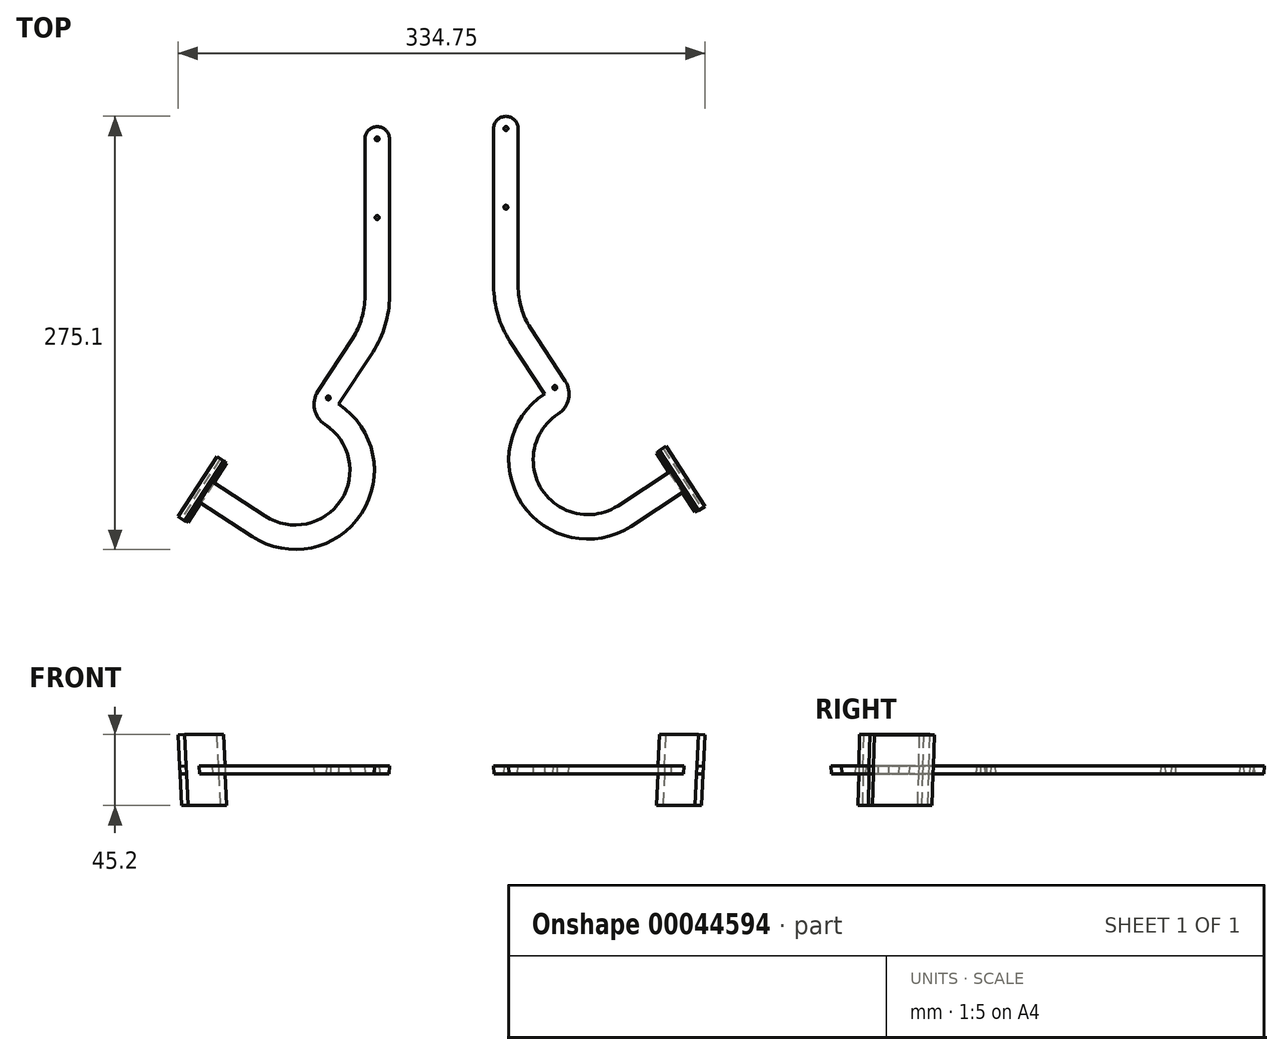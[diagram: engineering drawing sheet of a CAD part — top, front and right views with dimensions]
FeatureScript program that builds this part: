
annotation { "Feature Type Name" : "Feature", "Feature Type Description" : "" }
export const myFeature = defineFeature(function(context is Context, id is Id, definition is map)
    precondition{}
    {
        {
            var Q0;
            Q0=qCreatedBy(makeId("Top.planeOp"),FACE);
            var sketch = newSketch(context, id + "F0", { "sketchPlane" : qUnion([Q0])});
            skLineSegment(sketch, "E0", {"start": v(34.03, 89.45) * mm, "end": v(34.03, -10.55) * mm});
            skArc(sketch, "E1", {"start": v(34.03, -10.55) * mm, "mid": v(36.7, -28.86) * mm, "end": v(44.46, -45.66) * mm});
            skLineSegment(sketch, "E2", {"start": v(44.46, -45.66) * mm, "end": v(66.3, -79.17) * mm});
            skLineSegment(sketch, "E3", {"start": v(66.3, -79.17) * mm, "end": v(78.87, -70.98) * mm});
            skLineSegment(sketch, "E4", {"start": v(44.46, -45.66) * mm, "end": v(57.03, -37.47) * mm});
            skLineSegment(sketch, "E5", {"start": v(57.03, -37.47) * mm, "end": v(78.87, -70.98) * mm});
            skLineSegment(sketch, "E6", {"start": v(34.03, 89.45) * mm, "end": v(49.03, 89.45) * mm});
            skLineSegment(sketch, "E7", {"start": v(34.03, -10.55) * mm, "end": v(49.03, -10.55) * mm});
            skLineSegment(sketch, "E8", {"start": v(49.03, 89.45) * mm, "end": v(49.03, -10.55) * mm});
            skArc(sketch, "E9", {"start": v(49.03, -10.55) * mm, "mid": v(51.07, -24.6) * mm, "end": v(57.03, -37.47) * mm});
            skArc(sketch, "E10", {"start": v(49.03, 89.45) * mm, "mid": v(41.53, 96.95) * mm, "end": v(34.03, 89.45) * mm});
            skLineSegment(sketch, "E11", {"start": v(-32.73, 82.88) * mm, "end": v(-32.73, -17.12) * mm});
            skLineSegment(sketch, "E12", {"start": v(-32.73, 82.88) * mm, "end": v(-47.73, 82.88) * mm});
            skArc(sketch, "E13", {"start": v(-32.73, 82.88) * mm, "mid": v(-40.23, 90.38) * mm, "end": v(-47.73, 82.88) * mm});
            skLineSegment(sketch, "E14", {"start": v(-47.73, 82.88) * mm, "end": v(-47.73, -17.12) * mm});
            skLineSegment(sketch, "E15", {"start": v(-47.73, -17.12) * mm, "end": v(-32.73, -17.12) * mm});
            skArc(sketch, "E16", {"start": v(-32.73, -17.12) * mm, "mid": v(-35.39, -35.43) * mm, "end": v(-43.16, -52.23) * mm});
            skLineSegment(sketch, "E17", {"start": v(-43.16, -52.23) * mm, "end": v(-65, -85.74) * mm});
            skLineSegment(sketch, "E18", {"start": v(-65, -85.74) * mm, "end": v(-77.57, -77.55) * mm});
            skLineSegment(sketch, "E19", {"start": v(-43.16, -52.23) * mm, "end": v(-55.72, -44.04) * mm});
            skLineSegment(sketch, "E20", {"start": v(-55.72, -44.04) * mm, "end": v(-77.57, -77.55) * mm});
            skArc(sketch, "E21", {"start": v(-55.72, -44.04) * mm, "mid": v(-49.77, -31.16) * mm, "end": v(-47.73, -17.12) * mm});
            skPoint(sketch, "E22", {"position": v(-20.89, 95.2) * mm});
            skCircle(sketch, "E23", {"center": v(-40.23, 82.88) * mm, "radius": 1.5 * mm});
            skCircle(sketch, "E24", {"center": v(-71.28, -81.64) * mm, "radius": 1.5 * mm});
            skLineSegment(sketch, "E25", {"start": v(-40.23, 82.88) * mm, "end": v(-40.23, 32.88) * mm});
            skCircle(sketch, "E26", {"center": v(-40.23, 32.88) * mm, "radius": 1.5 * mm});
            skCircle(sketch, "E27", {"center": v(41.53, 89.45) * mm, "radius": 1.5 * mm});
            skLineSegment(sketch, "E28", {"start": v(41.53, 89.45) * mm, "end": v(41.53, 39.45) * mm});
            skCircle(sketch, "E29", {"center": v(41.53, 39.45) * mm, "radius": 1.5 * mm});
            skCircle(sketch, "E30", {"center": v(72.59, -75.08) * mm, "radius": 1.5 * mm});
            skLineSegment(sketch, "E31", {"start": v(-65, -85.74) * mm, "end": v(-73.19, -98.3) * mm});
            skArc(sketch, "E32", {"start": v(-77.57, -77.55) * mm, "mid": v(-79.68, -88.83) * mm, "end": v(-73.19, -98.3) * mm});
            skLineSegment(sketch, "E33", {"start": v(-73.19, -98.3) * mm, "end": v(-111.41, -156.95) * mm});
            skLineSegment(sketch, "E34", {"start": v(-111.41, -156.95) * mm, "end": v(-119.6, -169.51) * mm});
            skLineSegment(sketch, "E35", {"start": v(-111.41, -156.95) * mm, "end": v(-144.92, -135.1) * mm});
            skLineSegment(sketch, "E36", {"start": v(-144.92, -135.1) * mm, "end": v(-153.11, -147.67) * mm});
            skLineSegment(sketch, "E37", {"start": v(-119.6, -169.51) * mm, "end": v(-153.11, -147.67) * mm});
            skArc(sketch, "E38", {"start": v(-119.6, -169.51) * mm, "mid": v(-50.41, -154.93) * mm, "end": v(-65, -85.74) * mm});
            skArc(sketch, "E39", {"start": v(-111.41, -156.95) * mm, "mid": v(-62.98, -146.74) * mm, "end": v(-73.19, -98.3) * mm});
            skLineSegment(sketch, "E40", {"start": v(66.3, -79.17) * mm, "end": v(74.5, -91.74) * mm});
            skArc(sketch, "E41", {"start": v(74.5, -91.74) * mm, "mid": v(80.98, -82.27) * mm, "end": v(78.87, -70.98) * mm});
            skLineSegment(sketch, "E42", {"start": v(74.5, -91.74) * mm, "end": v(112.72, -150.38) * mm});
            skLineSegment(sketch, "E43", {"start": v(112.72, -150.38) * mm, "end": v(146.23, -128.54) * mm});
            skLineSegment(sketch, "E44", {"start": v(112.72, -150.38) * mm, "end": v(120.9, -162.95) * mm});
            skLineSegment(sketch, "E45", {"start": v(120.9, -162.95) * mm, "end": v(154.42, -141.1) * mm});
            skLineSegment(sketch, "E46", {"start": v(146.23, -128.54) * mm, "end": v(154.42, -141.1) * mm});
            skArc(sketch, "E47", {"start": v(66.3, -79.17) * mm, "mid": v(51.72, -148.36) * mm, "end": v(120.9, -162.95) * mm});
            skArc(sketch, "E48", {"start": v(74.5, -91.74) * mm, "mid": v(64.28, -140.17) * mm, "end": v(112.72, -150.38) * mm});
            skSolve(sketch);
        }
        {
            var Q0;
            {var subQ0=sQuery(id+"F0.wireOp",EDGE,"E13");Q0=makeQuery(id+"F0.imprint","IMPRINT",FACE,{"disambiguationData":[TD([[makeQuery(id+"F0.imprint","IMPRINT",EDGE,{"derivedFrom":subQ0}),1.0]])]});}
            var Q1;
            {var subQ4=sQuery(id+"F0.wireOp",EDGE,"E11");Q1=makeQuery(id+"F0.imprint","IMPRINT",FACE,{"disambiguationData":[TD([[makeQuery(id+"F0.imprint","IMPRINT",EDGE,{"derivedFrom":subQ4}),-1.0]])]});}
            var Q2;
            Q2=makeQuery(id+"F0.imprint","IMPRINT",FACE,{"disambiguationData":[TD([[makeQuery(id+"F0.imprint","IMPRINT",EDGE,{"derivedFrom":sQuery(id+"F0.wireOp",EDGE,"E15")}),-1.0]])]});
            var Q3;
            {var subQ5=sQuery(id+"F0.wireOp",EDGE,"E17");Q3=makeQuery(id+"F0.imprint","IMPRINT",FACE,{"disambiguationData":[TD([[makeQuery(id+"F0.imprint","IMPRINT",EDGE,{"derivedFrom":subQ5}),-1.0]])]});}
            var Q4;
            {var subQ4=sQuery(id+"F0.wireOp",EDGE,"E31");Q4=makeQuery(id+"F0.imprint","IMPRINT",FACE,{"disambiguationData":[TD([[makeQuery(id+"F0.imprint","IMPRINT",EDGE,{"derivedFrom":subQ4}),-1.0]])]});}
            var Q5;
            Q5=makeQuery(id+"F0.imprint","IMPRINT",FACE,{"disambiguationData":[TD([[makeQuery(id+"F0.imprint","IMPRINT",EDGE,{"derivedFrom":sQuery(id+"F0.wireOp",EDGE,"E31")}),1.0]])]});
            var Q6;
            Q6=makeQuery(id+"F0.imprint","IMPRINT",FACE,{"disambiguationData":[TD([[makeQuery(id+"F0.imprint","IMPRINT",EDGE,{"derivedFrom":sQuery(id+"F0.wireOp",EDGE,"E34")}),-1.0]])]});
            var Q7;
            {var subQ4=sQuery(id+"F0.wireOp",EDGE,"E10");Q7=makeQuery(id+"F0.imprint","IMPRINT",FACE,{"disambiguationData":[TD([[makeQuery(id+"F0.imprint","IMPRINT",EDGE,{"derivedFrom":subQ4}),1.0]])]});}
            var Q8;
            {var subQ6=sQuery(id+"F0.wireOp",EDGE,"E0");Q8=makeQuery(id+"F0.imprint","IMPRINT",FACE,{"disambiguationData":[TD([[makeQuery(id+"F0.imprint","IMPRINT",EDGE,{"derivedFrom":subQ6}),1.0]])]});}
            var Q9;
            Q9=makeQuery(id+"F0.imprint","IMPRINT",FACE,{"disambiguationData":[TD([[makeQuery(id+"F0.imprint","IMPRINT",EDGE,{"derivedFrom":sQuery(id+"F0.wireOp",EDGE,"E1")}),1.0]])]});
            var Q10;
            {var subQ1=sQuery(id+"F0.wireOp",EDGE,"E2");Q10=makeQuery(id+"F0.imprint","IMPRINT",FACE,{"disambiguationData":[TD([[makeQuery(id+"F0.imprint","IMPRINT",EDGE,{"derivedFrom":subQ1}),1.0]])]});}
            var Q11;
            {var subQ3=sQuery(id+"F0.wireOp",EDGE,"E40");Q11=makeQuery(id+"F0.imprint","IMPRINT",FACE,{"disambiguationData":[TD([[makeQuery(id+"F0.imprint","IMPRINT",EDGE,{"derivedFrom":subQ3}),1.0]])]});}
            var Q12;
            Q12=makeQuery(id+"F0.imprint","IMPRINT",FACE,{"disambiguationData":[TD([[makeQuery(id+"F0.imprint","IMPRINT",EDGE,{"derivedFrom":sQuery(id+"F0.wireOp",EDGE,"E40")}),-1.0]])]});
            var Q13;
            Q13=makeQuery(id+"F0.imprint","IMPRINT",FACE,{"disambiguationData":[TD([[makeQuery(id+"F0.imprint","IMPRINT",EDGE,{"derivedFrom":sQuery(id+"F0.wireOp",EDGE,"E43")}),-1.0]])]});
            extrude(context, id + "F1", {"entities" : qUnion([Q0, Q1, Q2, Q3, Q4, Q5, Q6, Q7, Q8, Q9, Q10, Q11, Q12, Q13]), "depth" : 5 * mm, "hasDraft" : true, "draftAngle" : 3 * degree});
        }
        {
            var Q0;
            Q0=makeQuery(id+"F1.opExtrude","SWEPT_FACE",FACE,{"disambiguationData":[OSD([sQuery(id+"F0.wireOp",EDGE,"E46")])]});
            var sketch = newSketch(context, id + "F2", { "sketchPlane" : qUnion([Q0])});
            skLineSegment(sketch, "E49", {"start": v(-186.9, 14.12) * mm, "end": v(-171.9, 13.61) * mm});
            skLineSegment(sketch, "E50", {"start": v(-202.41, 14.65) * mm, "end": v(-217.4, 15.17) * mm});
            skLineSegment(sketch, "E51", {"start": v(-187.33, 9.13) * mm, "end": v(-172.34, 8.62) * mm});
            skLineSegment(sketch, "E52", {"start": v(-202.32, 9.64) * mm, "end": v(-217.31, 10.15) * mm});
            skLineSegment(sketch, "E53", {"start": v(-171.9, 13.61) * mm, "end": v(-171.22, 33.6) * mm});
            skLineSegment(sketch, "E54", {"start": v(-171.22, 33.6) * mm, "end": v(-216.72, 35.15) * mm});
            skLineSegment(sketch, "E55", {"start": v(-217.4, 15.17) * mm, "end": v(-216.72, 35.15) * mm});
            skLineSegment(sketch, "E56", {"start": v(-172.34, 8.62) * mm, "end": v(-173.02, -11.37) * mm});
            skLineSegment(sketch, "E57", {"start": v(-173.02, -11.37) * mm, "end": v(-218, -9.84) * mm});
            skLineSegment(sketch, "E58", {"start": v(-217.31, 10.15) * mm, "end": v(-218, -9.84) * mm});
            skLineSegment(sketch, "E59", {"start": v(-217.4, 15.17) * mm, "end": v(-217.31, 10.15) * mm});
            skLineSegment(sketch, "E60", {"start": v(-171.9, 13.61) * mm, "end": v(-172.34, 8.62) * mm});
            skSolve(sketch);
        }
        {
            var Q0;
            Q0=makeQuery(id+"F2.imprint","IMPRINT",FACE,{"disambiguationData":[TD([[makeQuery(id+"F2.imprint","IMPRINT",EDGE,{"derivedFrom":sQuery(id+"F2.wireOp",EDGE,"E49")}),1.0]])]});
            var Q1;
            Q1=makeQuery(id+"F2.imprint","IMPRINT",FACE,{"disambiguationData":[TD([[makeQuery(id+"F2.imprint","IMPRINT",EDGE,{"derivedFrom":sQuery(id+"F2.wireOp",EDGE,"E50")}),1.0]])]});
            var Q2;
            Q2=makeQuery(id+"F2.imprint","IMPRINT",FACE,{"disambiguationData":[TD([[makeQuery(id+"F2.imprint","IMPRINT",EDGE,{"derivedFrom":sQuery(id+"F2.wireOp",EDGE,"E49")}),-1.0]])]});
            var Q3;
            {var subQ0=sQuery(id+"F0.wireOp",EDGE,"E46");Q3=makeQuery(id+"F2.imprint","IMPRINT",FACE,{"disambiguationData":[TD([[makeQuery(id+"F2.imprint","IMPRINT",EDGE,{"derivedFrom":makeQuery(id+"F1.opExtrude","CAP_EDGE",EDGE,{"disambiguationData":[OSD([subQ0])],"isStart":true})}),-1.0]])]});}
            var Q4;
            Q4=makeQuery(id+"F2.imprint","IMPRINT",FACE,{"disambiguationData":[TD([[makeQuery(id+"F2.imprint","IMPRINT",EDGE,{"derivedFrom":sQuery(id+"F2.wireOp",EDGE,"E51")}),-1.0]])]});
            extrude(context, id + "F3", {"entities" : qUnion([Q0, Q1, Q2, Q3, Q4]), "operationType" : NewBodyOperationType.ADD, "depth" : 5 * mm});
        }
        {
            var Q0;
            Q0=makeQuery(id+"F1.opExtrude","SWEPT_FACE",FACE,{"disambiguationData":[OSD([sQuery(id+"F0.wireOp",EDGE,"E36")])]});
            var sketch = newSketch(context, id + "F4", { "sketchPlane" : qUnion([Q0])});
            skLineSegment(sketch, "E61", {"start": v(207.2, 14.57) * mm, "end": v(191.69, 14.04) * mm});
            skLineSegment(sketch, "E62", {"start": v(191.69, 14.04) * mm, "end": v(176.7, 13.53) * mm});
            skLineSegment(sketch, "E63", {"start": v(207.2, 14.57) * mm, "end": v(222.2, 15.08) * mm});
            skLineSegment(sketch, "E64", {"start": v(207.11, 9.56) * mm, "end": v(222.1, 10.07) * mm});
            skLineSegment(sketch, "E65", {"start": v(192.12, 9.05) * mm, "end": v(177.13, 8.54) * mm});
            skLineSegment(sketch, "E66", {"start": v(177.13, 8.54) * mm, "end": v(177.81, -11.45) * mm});
            skLineSegment(sketch, "E67", {"start": v(177.81, -11.45) * mm, "end": v(222.79, -9.92) * mm});
            skLineSegment(sketch, "E68", {"start": v(222.1, 10.07) * mm, "end": v(222.79, -9.92) * mm});
            skLineSegment(sketch, "E69", {"start": v(222.2, 15.08) * mm, "end": v(221.51, 35.07) * mm});
            skLineSegment(sketch, "E70", {"start": v(221.51, 35.07) * mm, "end": v(176.02, 33.52) * mm});
            skLineSegment(sketch, "E71", {"start": v(176.7, 13.53) * mm, "end": v(176.02, 33.52) * mm});
            skLineSegment(sketch, "E72", {"start": v(222.2, 15.08) * mm, "end": v(222.1, 10.07) * mm});
            skLineSegment(sketch, "E73", {"start": v(176.7, 13.53) * mm, "end": v(177.13, 8.54) * mm});
            skSolve(sketch);
        }
        {
            var Q0;
            Q0=makeQuery(id+"F4.imprint","IMPRINT",FACE,{"disambiguationData":[TD([[makeQuery(id+"F4.imprint","IMPRINT",EDGE,{"derivedFrom":sQuery(id+"F4.wireOp",EDGE,"E61")}),1.0]])]});
            var Q1;
            Q1=makeQuery(id+"F4.imprint","IMPRINT",FACE,{"disambiguationData":[TD([[makeQuery(id+"F4.imprint","IMPRINT",EDGE,{"derivedFrom":sQuery(id+"F4.wireOp",EDGE,"E63")}),-1.0]])]});
            var Q2;
            Q2=makeQuery(id+"F4.imprint","IMPRINT",FACE,{"disambiguationData":[TD([[makeQuery(id+"F4.imprint","IMPRINT",EDGE,{"derivedFrom":sQuery(id+"F4.wireOp",EDGE,"E64")}),-1.0]])]});
            var Q3;
            Q3=makeQuery(id+"F4.imprint","IMPRINT",FACE,{"disambiguationData":[TD([[makeQuery(id+"F4.imprint","IMPRINT",EDGE,{"derivedFrom":sQuery(id+"F4.wireOp",EDGE,"E62")}),1.0]])]});
            var Q4;
            Q4=makeQuery(id+"F4.imprint","IMPRINT",FACE,{"disambiguationData":[TD([[makeQuery(id+"F4.imprint","IMPRINT",EDGE,{"derivedFrom":sQuery(id+"F4.wireOp",EDGE,"E61")}),-1.0]])]});
            extrude(context, id + "F5", {"entities" : qUnion([Q0, Q1, Q2, Q3, Q4]), "operationType" : NewBodyOperationType.ADD, "depth" : 5 * mm});
        }
    });
